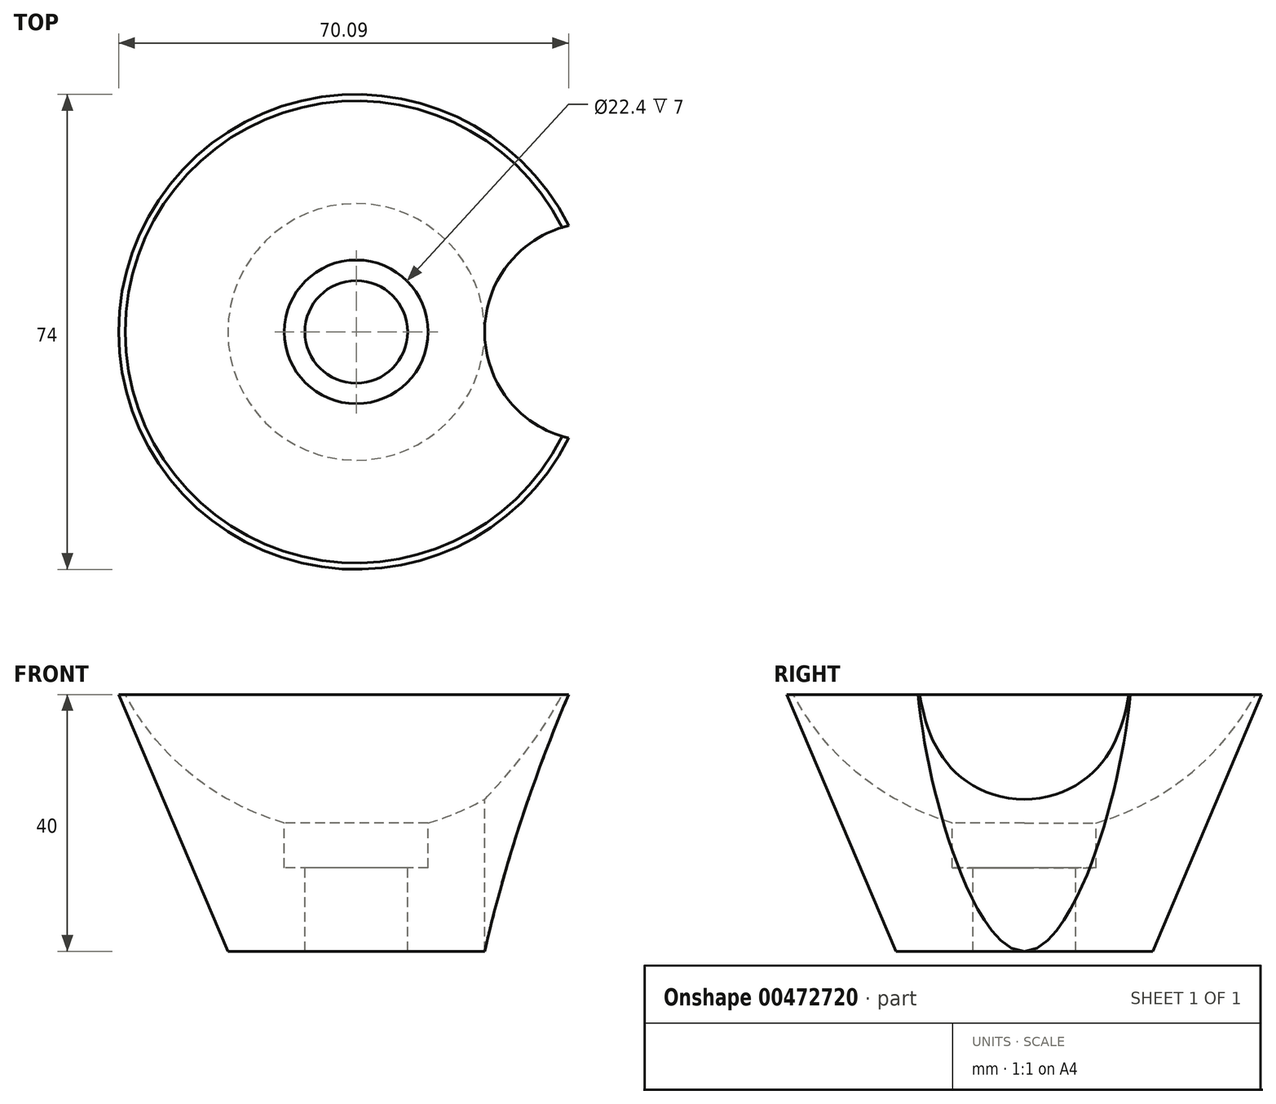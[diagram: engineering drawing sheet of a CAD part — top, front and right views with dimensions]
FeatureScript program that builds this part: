
annotation { "Feature Type Name" : "Feature", "Feature Type Description" : "" }
export const myFeature = defineFeature(function(context is Context, id is Id, definition is map)
    precondition{}
    {
        {
            var Q0;
            Q0=qCreatedBy(makeId("Top.planeOp"),FACE);
            var sketch = newSketch(context, id + "F0", { "sketchPlane" : qUnion([Q0])});
            skCircle(sketch, "E0", {"center": v(0, 0) * mm, "radius": 11.2 * mm});
            skCircle(sketch, "E1", {"center": v(0, 0) * mm, "radius": 20 * mm});
            skCircle(sketch, "E2", {"center": v(0, 0) * mm, "radius": 8 * mm});
            skSolve(sketch);
        }
        {
            var Q0;
            Q0=makeQuery(id+"F0.imprint","IMPRINT",FACE,{"disambiguationData":[TD([[makeQuery(id+"F0.imprint","IMPRINT",EDGE,{"derivedFrom":sQuery(id+"F0.wireOp",EDGE,"E0")}),-1.0]])]});
            var Q1;
            Q1=makeQuery(id+"F0.imprint","IMPRINT",FACE,{"disambiguationData":[TD([[makeQuery(id+"F0.imprint","IMPRINT",EDGE,{"derivedFrom":sQuery(id+"F0.wireOp",EDGE,"E0")}),1.0]])]});
            extrude(context, id + "F1", {"entities" : qUnion([Q0, Q1]), "oppositeDirection" : true, "depth" : 20 * mm});
        }
        {
            var Q0;
            Q0=makeQuery(id+"F0.imprint","IMPRINT",FACE,{"disambiguationData":[TD([[makeQuery(id+"F0.imprint","IMPRINT",EDGE,{"derivedFrom":sQuery(id+"F0.wireOp",EDGE,"E0")}),1.0]])]});
            extrude(context, id + "F2", {"entities" : qUnion([Q0]), "operationType" : NewBodyOperationType.REMOVE, "oppositeDirection" : true, "depth" : 7 * mm});
        }
        {
            var Q0;
            Q0=qCreatedBy(makeId("Front.planeOp"),FACE);
            var sketch = newSketch(context, id + "F3", { "sketchPlane" : qUnion([Q0])});
            skLineSegment(sketch, "E3.0", {"start": v(-20, 0) * mm, "end": v(20, 0) * mm, "construction": true});
            skLineSegment(sketch, "E4.0", {"start": v(-20, -20) * mm, "end": v(20, -20) * mm, "construction": true});
            skLineSegment(sketch, "E5", {"start": v(-20, -20) * mm, "end": v(-37, 20) * mm});
            skLineSegment(sketch, "E6", {"start": v(-11.2, 20) * mm, "end": v(-11.2, -20) * mm, "construction": true});
            skPoint(sketch, "E7", {"position": v(-28.5, 0) * mm});
            skLineSegment(sketch, "E8", {"start": v(-36, 20) * mm, "end": v(-37, 20) * mm});
            skLineSegment(sketch, "E9", {"start": v(-11.2, 0) * mm, "end": v(-11.2, -20) * mm});
            skLineSegment(sketch, "E10", {"start": v(-20, -20) * mm, "end": v(-11.2, -20) * mm});
            skArc(sketch, "E11", {"start": v(-36, 20) * mm, "mid": v(-25.62, 7.5) * mm, "end": v(-11.2, 0) * mm});
            skSolve(sketch);
        }
        {
            var Q0;
            Q0=makeQuery(id+"F3.imprint","IMPRINT",FACE,{"disambiguationData":[TD([[makeQuery(id+"F3.imprint","IMPRINT",EDGE,{"derivedFrom":sQuery(id+"F3.wireOp",EDGE,"E5")}),-1.0]])]});
            var Q1;
            Q1=sQuery(id+"F0.wireOp",EDGE,"E0");
            revolve(context, id + "F4", {"operationType" : NewBodyOperationType.ADD, "entities" : qUnion([Q0]), "axis" : qUnion([Q1]), "revolveType" : RevolveType.FULL});
        }
        {
            var Q0;
            Q0=makeQuery(id+"F4.opRevolve","SWEPT_FACE",FACE,{"disambiguationData":[OSD([sQuery(id+"F3.wireOp",EDGE,"E8")])]});
            var sketch = newSketch(context, id + "F5", { "sketchPlane" : qUnion([Q0])});
            skCircle(sketch, "E12.0", {"center": v(0, 0) * mm, "radius": 37 * mm, "construction": true});
            skCircle(sketch, "E13", {"center": v(37, 0) * mm, "radius": 17 * mm});
            skCircle(sketch, "E14.0", {"center": v(0, 0) * mm, "radius": 20 * mm, "construction": true});
            skSolve(sketch);
        }
        {
            var Q0;
            Q0 = qSketchRegion(id + "F5", true);
            extrude(context, id + "F6", {"entities" : qUnion([Q0]), "operationType" : NewBodyOperationType.REMOVE, "endBound" : BoundingType.THROUGH_ALL, "oppositeDirection" : true, "depth" : 25 * mm});
        }
    });
